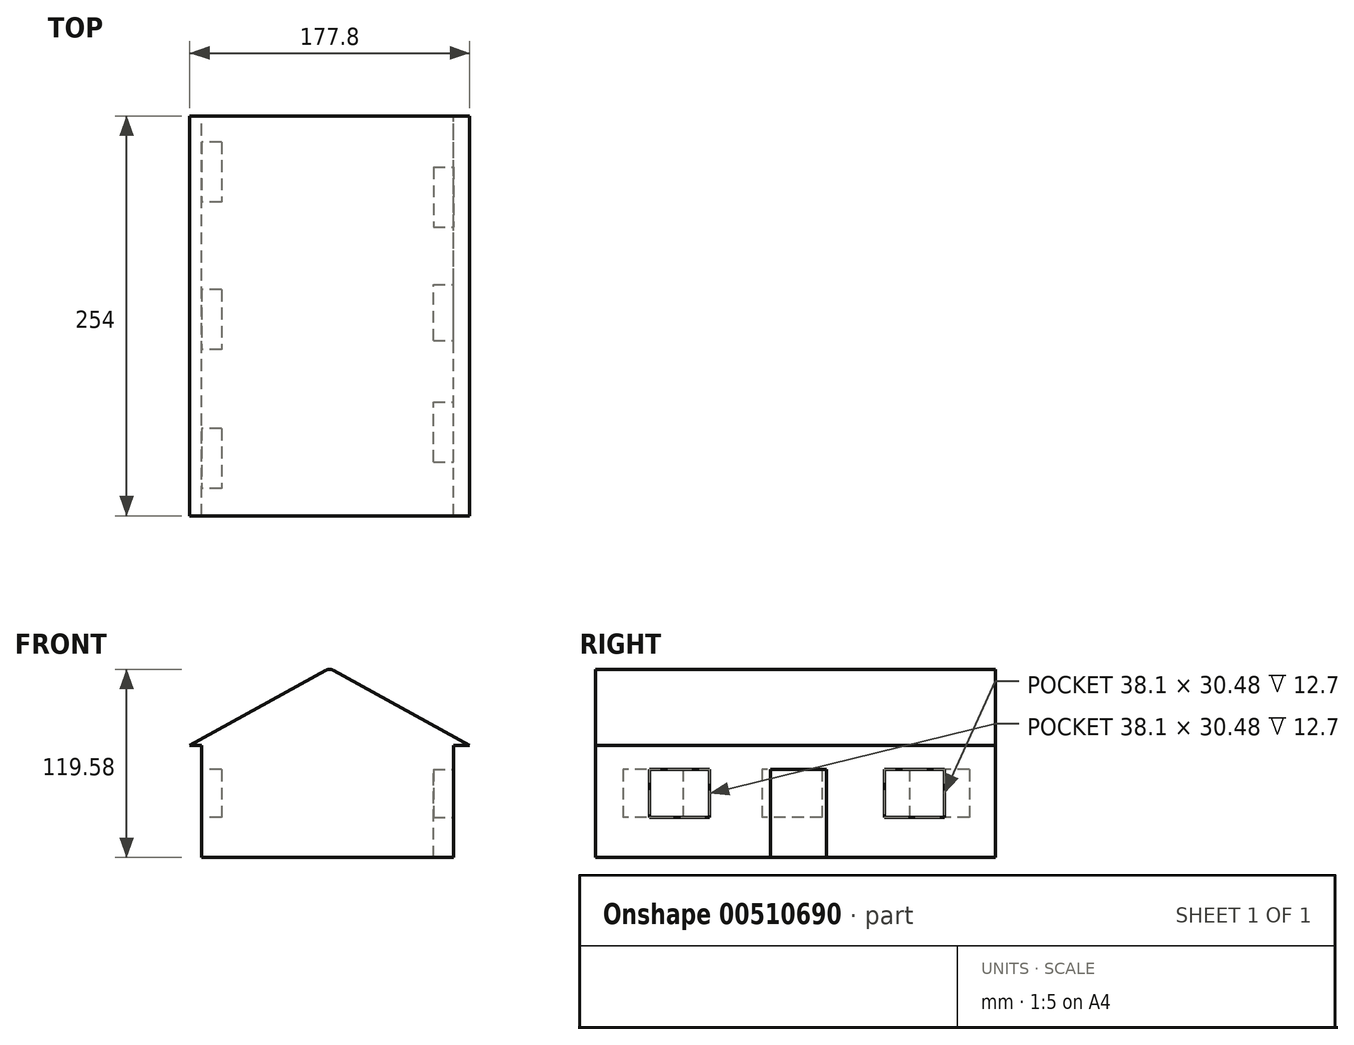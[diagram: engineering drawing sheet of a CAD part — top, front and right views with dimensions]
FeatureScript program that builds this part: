
annotation { "Feature Type Name" : "Feature", "Feature Type Description" : "" }
export const myFeature = defineFeature(function(context is Context, id is Id, definition is map)
    precondition{}
    {
        {
            var Q0;
            Q0=qCreatedBy(makeId("Front.planeOp"),FACE);
            var sketch = newSketch(context, id + "F0", { "sketchPlane" : qUnion([Q0])});
            skLineSegment(sketch, "E0", {"start": v(-81.48, -63.91) * mm, "end": v(78.54, -63.91) * mm});
            skLineSegment(sketch, "E1", {"start": v(78.54, -63.91) * mm, "end": v(78.54, 7.2) * mm});
            skLineSegment(sketch, "E2", {"start": v(-81.48, 7.2) * mm, "end": v(78.54, 7.2) * mm});
            skLineSegment(sketch, "E3", {"start": v(-88.9, 7.2) * mm, "end": v(0, 56.4) * mm});
            skLineSegment(sketch, "E4", {"start": v(0, 56.4) * mm, "end": v(88.9, 7.2) * mm});
            skLineSegment(sketch, "E5", {"start": v(-81.48, 7.2) * mm, "end": v(-81.48, -63.91) * mm});
            skLineSegment(sketch, "E6", {"start": v(88.9, 7.2) * mm, "end": v(-88.9, 7.2) * mm});
            skSolve(sketch);
        }
        {
            var Q0;
            Q0=makeQuery(id+"F0.imprint","IMPRINT",FACE,{"disambiguationData":[TD([[makeQuery(id+"F0.imprint","IMPRINT",EDGE,{"derivedFrom":sQuery(id+"F0.wireOp",EDGE,"E0")}),1.0]])]});
            var Q1;
            {var subQ4=sQuery(id+"F0.wireOp",EDGE,"E3");Q1=makeQuery(id+"F0.imprint","IMPRINT",FACE,{"disambiguationData":[TD([[makeQuery(id+"F0.imprint","IMPRINT",EDGE,{"derivedFrom":subQ4}),-1.0]])]});}
            var Q2;
            Q2=sQuery(id+"F0.wireOp",EDGE,"E3");
            var Q3;
            Q3=sQuery(id+"F0.wireOp",EDGE,"E4");
            var Q4;
            Q4=sQuery(id+"F0.wireOp",EDGE,"E1");
            var Q5;
            Q5=sQuery(id+"F0.wireOp",EDGE,"E6");
            var Q6;
            Q6=sQuery(id+"F0.wireOp",EDGE,"E2");
            extrude(context, id + "F1", {"entities" : qUnion([Q0, Q1]), "surfaceEntities" : qUnion([Q2, Q3, Q4, Q5, Q6]), "depth" : 254 * mm});
        }
        {
            var Q0;
            Q0=makeQuery(id+"F1.opExtrude","SWEPT_FACE",FACE,{"disambiguationData":[OSD([sQuery(id+"F0.wireOp",EDGE,"E1")])]});
            var sketch = newSketch(context, id + "F2", { "sketchPlane" : qUnion([Q0])});
            skLineSegment(sketch, "E7.bottom", {"start": v(-219.81, -8.03) * mm, "end": v(-181.71, -8.03) * mm});
            skLineSegment(sketch, "E7.top", {"start": v(-219.81, -38.51) * mm, "end": v(-181.71, -38.51) * mm});
            skLineSegment(sketch, "E7.left", {"start": v(-219.81, -8.03) * mm, "end": v(-219.81, -38.51) * mm});
            skLineSegment(sketch, "E7.right", {"start": v(-181.71, -8.03) * mm, "end": v(-181.71, -38.51) * mm});
            skLineSegment(sketch, "E8.bottom", {"start": v(-32.6, -8.03) * mm, "end": v(-70.7, -8.03) * mm});
            skLineSegment(sketch, "E8.top", {"start": v(-32.6, -38.51) * mm, "end": v(-70.7, -38.51) * mm});
            skLineSegment(sketch, "E8.left", {"start": v(-32.6, -8.03) * mm, "end": v(-32.6, -38.51) * mm});
            skLineSegment(sketch, "E8.right", {"start": v(-70.7, -8.03) * mm, "end": v(-70.7, -38.51) * mm});
            skLineSegment(sketch, "E9.bottom", {"start": v(-142.8, -63.91) * mm, "end": v(-107.25, -63.91) * mm});
            skLineSegment(sketch, "E9.top", {"start": v(-142.8, -8.03) * mm, "end": v(-107.25, -8.03) * mm});
            skLineSegment(sketch, "E9.left", {"start": v(-142.8, -63.91) * mm, "end": v(-142.8, -8.03) * mm});
            skLineSegment(sketch, "E9.right", {"start": v(-107.25, -63.91) * mm, "end": v(-107.25, -8.03) * mm});
            skSolve(sketch);
        }
        {
            var Q0;
            Q0 = qSketchRegion(id + "F2", true);
            extrude(context, id + "F3", {"entities" : qUnion([Q0]), "operationType" : NewBodyOperationType.REMOVE, "oppositeDirection" : true, "depth" : 12.7 * mm});
        }
        {
            var Q0;
            Q0=makeQuery(id+"F1.opExtrude","SWEPT_FACE",FACE,{"disambiguationData":[OSD([sQuery(id+"F0.wireOp",EDGE,"E5")])]});
            var sketch = newSketch(context, id + "F4", { "sketchPlane" : qUnion([Q0])});
            skSolve(sketch);
        }
        {
            var Q0;
            {var subQ0=sQuery(id+"F0.wireOp",EDGE,"E5");Q0=makeQuery(id+"F4.imprint","IMPRINT",FACE,{"disambiguationData":[TD([[makeQuery(id+"F4.imprint","IMPRINT",EDGE,{"derivedFrom":makeQuery(id+"F1.opExtrude","CAP_EDGE",EDGE,{"disambiguationData":[OSD([subQ0])],"isStart":true})}),1.0]])]});}
            var sketch = newSketch(context, id + "F5", { "sketchPlane" : qUnion([Q0])});
            skLineSegment(sketch, "E10.bottom", {"start": v(16.67, -8.03) * mm, "end": v(54.77, -8.03) * mm});
            skLineSegment(sketch, "E10.top", {"start": v(16.67, -38.51) * mm, "end": v(54.77, -38.51) * mm});
            skLineSegment(sketch, "E10.left", {"start": v(16.67, -8.03) * mm, "end": v(16.67, -38.51) * mm});
            skLineSegment(sketch, "E10.right", {"start": v(54.77, -8.03) * mm, "end": v(54.77, -38.51) * mm});
            skLineSegment(sketch, "E11.bottom", {"start": v(110.3, -8.03) * mm, "end": v(148.4, -8.03) * mm});
            skLineSegment(sketch, "E11.top", {"start": v(110.3, -38.51) * mm, "end": v(148.4, -38.51) * mm});
            skLineSegment(sketch, "E11.left", {"start": v(110.3, -8.03) * mm, "end": v(110.3, -38.51) * mm});
            skLineSegment(sketch, "E11.right", {"start": v(148.4, -8.03) * mm, "end": v(148.4, -38.51) * mm});
            skLineSegment(sketch, "E12.bottom", {"start": v(198.57, -8.03) * mm, "end": v(236.67, -8.03) * mm});
            skLineSegment(sketch, "E12.top", {"start": v(198.57, -38.51) * mm, "end": v(236.67, -38.51) * mm});
            skLineSegment(sketch, "E12.left", {"start": v(198.57, -8.03) * mm, "end": v(198.57, -38.51) * mm});
            skLineSegment(sketch, "E12.right", {"start": v(236.67, -8.03) * mm, "end": v(236.67, -38.51) * mm});
            skSolve(sketch);
        }
        {
            var Q0;
            Q0 = qSketchRegion(id + "F5", true);
            extrude(context, id + "F6", {"entities" : qUnion([Q0]), "operationType" : NewBodyOperationType.REMOVE, "oppositeDirection" : true, "depth" : 12.7 * mm});
        }
        {
            var Q0;
            Q0=makeQuery(id+"F1.opExtrude","SWEPT_EDGE",EDGE,{"disambiguationData":[OSD([sQuery(id+"F0.wireOp",EDGE,"E3"),sQuery(id+"F0.wireOp",EDGE,"E4")])]});
            fillet(context, id + "F7", {"entities" : qUnion([Q0]), "radius" : 5.08 * mm, "tangentPropagation" : true, "allowEdgeOverflow" : false});
        }
    });
